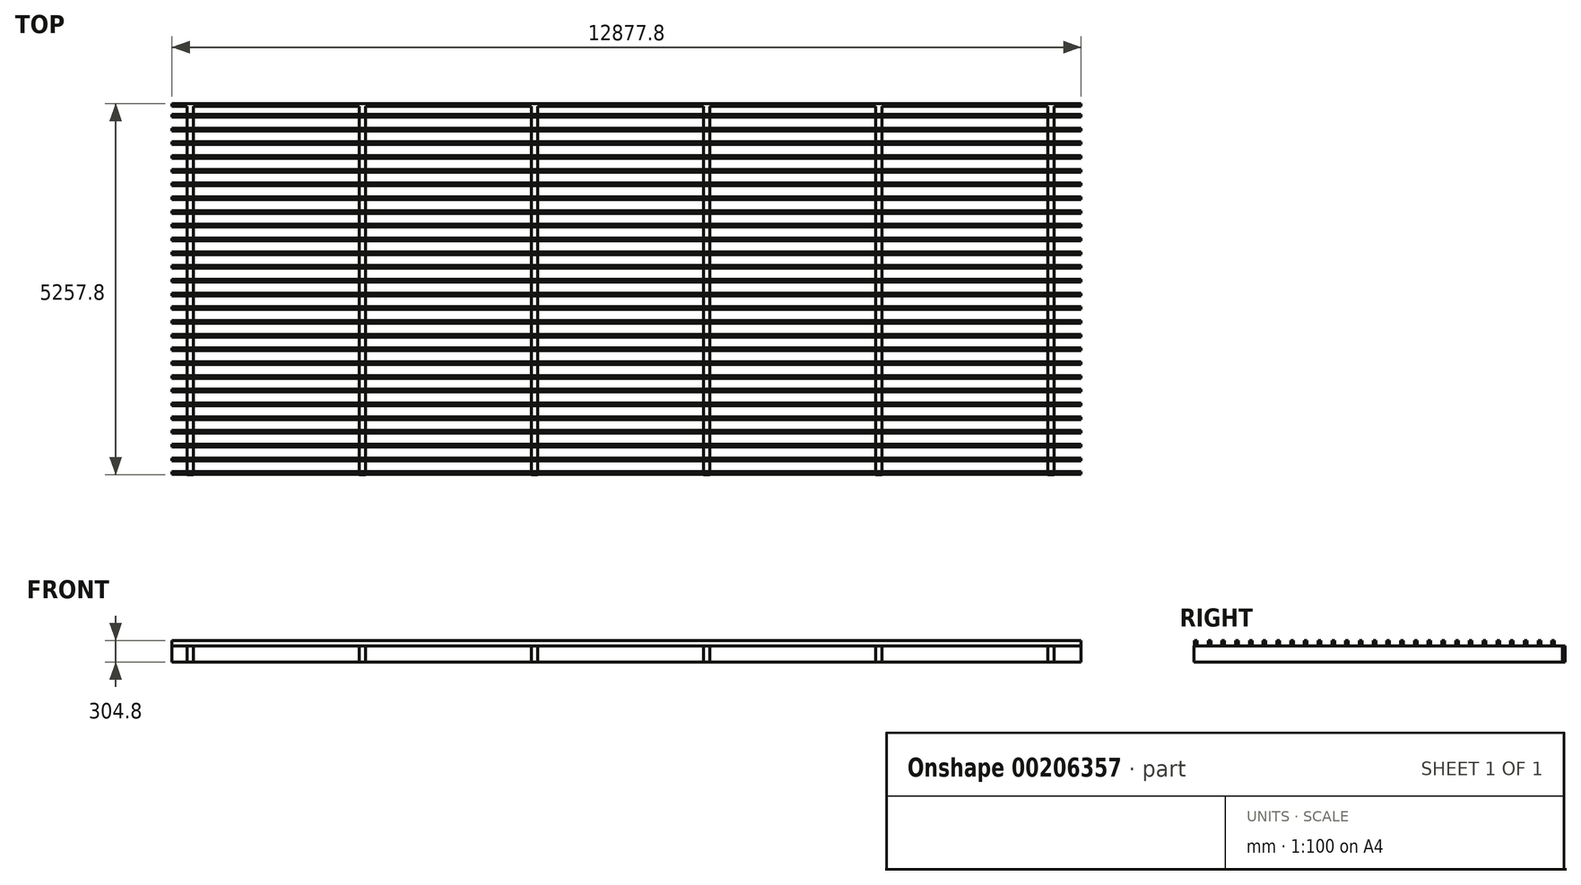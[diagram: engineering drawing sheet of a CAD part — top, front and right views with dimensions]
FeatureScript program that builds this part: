
annotation { "Feature Type Name" : "Feature", "Feature Type Description" : "" }
export const myFeature = defineFeature(function(context is Context, id is Id, definition is map)
    precondition{}
    {
        {
            var Q0;
            Q0=qCreatedBy(makeId("Front.planeOp"),FACE);
            var sketch = newSketch(context, id + "F0", { "sketchPlane" : qUnion([Q0])});
            skLineSegment(sketch, "E0.bottom", {"start": v(6438.9, -114.3) * mm, "end": v(-6438.9, -114.3) * mm});
            skLineSegment(sketch, "E0.top", {"start": v(6438.9, 114.3) * mm, "end": v(-6438.9, 114.3) * mm});
            skLineSegment(sketch, "E0.left", {"start": v(6438.9, -114.3) * mm, "end": v(6438.9, 114.3) * mm});
            skLineSegment(sketch, "E0.right", {"start": v(-6438.9, -114.3) * mm, "end": v(-6438.9, 114.3) * mm});
            skPoint(sketch, "E0.middle", {"position": v(0, 0) * mm});
            skSolve(sketch);
        }
        {
            var Q0;
            Q0 = qSketchRegion(id + "F0", true);
            extrude(context, id + "F1", {"entities" : qUnion([Q0]), "oppositeDirection" : true, "depth" : 38.1 * mm});
        }
        {
            var Q0;
            Q0=makeQuery(id+"F1.opExtrude","CAP_FACE",FACE,{"disambiguationData":[OSD([sQuery(id+"F0.wireOp",EDGE,"E0.bottom"),sQuery(id+"F0.wireOp",EDGE,"E0.top"),sQuery(id+"F0.wireOp",EDGE,"E0.left"),sQuery(id+"F0.wireOp",EDGE,"E0.right")])],"isStart":true});
            var sketch = newSketch(context, id + "F2", { "sketchPlane" : qUnion([Q0])});
            skLineSegment(sketch, "E1.bottom", {"start": v(6057.9, 114.3) * mm, "end": v(5969, 114.3) * mm});
            skLineSegment(sketch, "E1.top", {"start": v(6057.9, -114.3) * mm, "end": v(5969, -114.3) * mm});
            skLineSegment(sketch, "E1.left", {"start": v(6057.9, 114.3) * mm, "end": v(6057.9, -114.3) * mm});
            skLineSegment(sketch, "E1.right", {"start": v(5969, 114.3) * mm, "end": v(5969, -114.3) * mm});
            skLineSegment(sketch, "E2.1.0.0", {"start": v(3619.5, 114.3) * mm, "end": v(3530.6, 114.3) * mm});
            skLineSegment(sketch, "E2.1.0.1", {"start": v(3530.6, 114.3) * mm, "end": v(3530.6, -114.3) * mm});
            skLineSegment(sketch, "E2.1.0.2", {"start": v(3619.5, 114.3) * mm, "end": v(3619.5, -114.3) * mm});
            skLineSegment(sketch, "E2.1.0.3", {"start": v(3619.5, -114.3) * mm, "end": v(3530.6, -114.3) * mm});
            skLineSegment(sketch, "E2.2.0.0", {"start": v(1181.1, 114.3) * mm, "end": v(1092.2, 114.3) * mm});
            skLineSegment(sketch, "E2.2.0.1", {"start": v(1092.2, 114.3) * mm, "end": v(1092.2, -114.3) * mm});
            skLineSegment(sketch, "E2.2.0.2", {"start": v(1181.1, 114.3) * mm, "end": v(1181.1, -114.3) * mm});
            skLineSegment(sketch, "E2.2.0.3", {"start": v(1181.1, -114.3) * mm, "end": v(1092.2, -114.3) * mm});
            skLineSegment(sketch, "E2.3.0.0", {"start": v(-1257.3, 114.3) * mm, "end": v(-1346.2, 114.3) * mm});
            skLineSegment(sketch, "E2.3.0.1", {"start": v(-1346.2, 114.3) * mm, "end": v(-1346.2, -114.3) * mm});
            skLineSegment(sketch, "E2.3.0.2", {"start": v(-1257.3, 114.3) * mm, "end": v(-1257.3, -114.3) * mm});
            skLineSegment(sketch, "E2.3.0.3", {"start": v(-1257.3, -114.3) * mm, "end": v(-1346.2, -114.3) * mm});
            skLineSegment(sketch, "E2.4.0.0", {"start": v(-3695.7, 114.3) * mm, "end": v(-3784.6, 114.3) * mm});
            skLineSegment(sketch, "E2.4.0.1", {"start": v(-3784.6, 114.3) * mm, "end": v(-3784.6, -114.3) * mm});
            skLineSegment(sketch, "E2.4.0.2", {"start": v(-3695.7, 114.3) * mm, "end": v(-3695.7, -114.3) * mm});
            skLineSegment(sketch, "E2.4.0.3", {"start": v(-3695.7, -114.3) * mm, "end": v(-3784.6, -114.3) * mm});
            skLineSegment(sketch, "E2.5.0.0", {"start": v(-6134.1, 114.3) * mm, "end": v(-6223, 114.3) * mm});
            skLineSegment(sketch, "E2.5.0.1", {"start": v(-6223, 114.3) * mm, "end": v(-6223, -114.3) * mm});
            skLineSegment(sketch, "E2.5.0.2", {"start": v(-6134.1, 114.3) * mm, "end": v(-6134.1, -114.3) * mm});
            skLineSegment(sketch, "E2.5.0.3", {"start": v(-6134.1, -114.3) * mm, "end": v(-6223, -114.3) * mm});
            skLineSegment(sketch, "E2.direction1", {"start": v(5969, 114.3) * mm, "end": v(3530.6, 114.3) * mm, "construction": true});
            skSolve(sketch);
        }
        {
            var Q0;
            Q0=makeQuery(id+"F2.imprint","IMPRINT",FACE,{"disambiguationData":[TD([[makeQuery(id+"F2.imprint","IMPRINT",EDGE,{"derivedFrom":sQuery(id+"F2.wireOp",EDGE,"E2.5.0.0")}),1.0]])]});
            var Q1;
            Q1=makeQuery(id+"F2.imprint","IMPRINT",FACE,{"disambiguationData":[TD([[makeQuery(id+"F2.imprint","IMPRINT",EDGE,{"derivedFrom":sQuery(id+"F2.wireOp",EDGE,"E2.4.0.0")}),1.0]])]});
            var Q2;
            Q2=makeQuery(id+"F2.imprint","IMPRINT",FACE,{"disambiguationData":[TD([[makeQuery(id+"F2.imprint","IMPRINT",EDGE,{"derivedFrom":sQuery(id+"F2.wireOp",EDGE,"E2.3.0.0")}),1.0]])]});
            var Q3;
            Q3=makeQuery(id+"F2.imprint","IMPRINT",FACE,{"disambiguationData":[TD([[makeQuery(id+"F2.imprint","IMPRINT",EDGE,{"derivedFrom":sQuery(id+"F2.wireOp",EDGE,"E2.2.0.0")}),1.0]])]});
            var Q4;
            Q4=makeQuery(id+"F2.imprint","IMPRINT",FACE,{"disambiguationData":[TD([[makeQuery(id+"F2.imprint","IMPRINT",EDGE,{"derivedFrom":sQuery(id+"F2.wireOp",EDGE,"E2.1.0.0")}),1.0]])]});
            var Q5;
            Q5=makeQuery(id+"F2.imprint","IMPRINT",FACE,{"disambiguationData":[TD([[makeQuery(id+"F2.imprint","IMPRINT",EDGE,{"derivedFrom":sQuery(id+"F2.wireOp",EDGE,"E1.bottom")}),1.0]])]});
            extrude(context, id + "F3", {"entities" : qUnion([Q0, Q1, Q2, Q3, Q4, Q5]), "operationType" : NewBodyOperationType.ADD, "depth" : 5219.7 * mm});
        }
        {
            var Q0;
            Q0=makeQuery(id+"F1.opExtrude","SWEPT_FACE",FACE,{"disambiguationData":[OSD([sQuery(id+"F0.wireOp",EDGE,"E0.left")])]});
            var sketch = newSketch(context, id + "F4", { "sketchPlane" : qUnion([Q0])});
            skLineSegment(sketch, "E3.bottom", {"start": v(-152.4, 190.5) * mm, "end": v(-114.3, 190.5) * mm});
            skLineSegment(sketch, "E3.top", {"start": v(-152.4, 114.3) * mm, "end": v(-114.3, 114.3) * mm});
            skLineSegment(sketch, "E3.left", {"start": v(-152.4, 190.5) * mm, "end": v(-152.4, 114.3) * mm});
            skLineSegment(sketch, "E3.right", {"start": v(-114.3, 190.5) * mm, "end": v(-114.3, 114.3) * mm});
            skLineSegment(sketch, "E4.1.0.0", {"start": v(-347.14, 190.5) * mm, "end": v(-309.04, 190.5) * mm});
            skLineSegment(sketch, "E4.1.0.1", {"start": v(-347.14, 190.5) * mm, "end": v(-347.14, 114.3) * mm});
            skLineSegment(sketch, "E4.1.0.2", {"start": v(-347.14, 114.3) * mm, "end": v(-309.04, 114.3) * mm});
            skLineSegment(sketch, "E4.1.0.3", {"start": v(-309.04, 190.5) * mm, "end": v(-309.04, 114.3) * mm});
            skLineSegment(sketch, "E4.2.0.0", {"start": v(-541.88, 190.5) * mm, "end": v(-503.78, 190.5) * mm});
            skLineSegment(sketch, "E4.2.0.1", {"start": v(-541.88, 190.5) * mm, "end": v(-541.88, 114.3) * mm});
            skLineSegment(sketch, "E4.2.0.2", {"start": v(-541.88, 114.3) * mm, "end": v(-503.78, 114.3) * mm});
            skLineSegment(sketch, "E4.2.0.3", {"start": v(-503.78, 190.5) * mm, "end": v(-503.78, 114.3) * mm});
            skLineSegment(sketch, "E4.3.0.0", {"start": v(-736.63, 190.5) * mm, "end": v(-698.53, 190.5) * mm});
            skLineSegment(sketch, "E4.3.0.1", {"start": v(-736.63, 190.5) * mm, "end": v(-736.63, 114.3) * mm});
            skLineSegment(sketch, "E4.3.0.2", {"start": v(-736.63, 114.3) * mm, "end": v(-698.53, 114.3) * mm});
            skLineSegment(sketch, "E4.3.0.3", {"start": v(-698.53, 190.5) * mm, "end": v(-698.53, 114.3) * mm});
            skLineSegment(sketch, "E4.4.0.0", {"start": v(-931.37, 190.5) * mm, "end": v(-893.27, 190.5) * mm});
            skLineSegment(sketch, "E4.4.0.1", {"start": v(-931.37, 190.5) * mm, "end": v(-931.37, 114.3) * mm});
            skLineSegment(sketch, "E4.4.0.2", {"start": v(-931.37, 114.3) * mm, "end": v(-893.27, 114.3) * mm});
            skLineSegment(sketch, "E4.4.0.3", {"start": v(-893.27, 190.5) * mm, "end": v(-893.27, 114.3) * mm});
            skLineSegment(sketch, "E4.5.0.0", {"start": v(-1126.1, 190.5) * mm, "end": v(-1088, 190.5) * mm});
            skLineSegment(sketch, "E4.5.0.1", {"start": v(-1126.1, 190.5) * mm, "end": v(-1126.1, 114.3) * mm});
            skLineSegment(sketch, "E4.5.0.2", {"start": v(-1126.1, 114.3) * mm, "end": v(-1088, 114.3) * mm});
            skLineSegment(sketch, "E4.5.0.3", {"start": v(-1088, 190.5) * mm, "end": v(-1088, 114.3) * mm});
            skLineSegment(sketch, "E4.6.0.0", {"start": v(-1320.85, 190.5) * mm, "end": v(-1282.75, 190.5) * mm});
            skLineSegment(sketch, "E4.6.0.1", {"start": v(-1320.85, 190.5) * mm, "end": v(-1320.85, 114.3) * mm});
            skLineSegment(sketch, "E4.6.0.2", {"start": v(-1320.85, 114.3) * mm, "end": v(-1282.75, 114.3) * mm});
            skLineSegment(sketch, "E4.6.0.3", {"start": v(-1282.75, 190.5) * mm, "end": v(-1282.75, 114.3) * mm});
            skLineSegment(sketch, "E4.7.0.0", {"start": v(-1515.6, 190.5) * mm, "end": v(-1477.5, 190.5) * mm});
            skLineSegment(sketch, "E4.7.0.1", {"start": v(-1515.6, 190.5) * mm, "end": v(-1515.6, 114.3) * mm});
            skLineSegment(sketch, "E4.7.0.2", {"start": v(-1515.6, 114.3) * mm, "end": v(-1477.5, 114.3) * mm});
            skLineSegment(sketch, "E4.7.0.3", {"start": v(-1477.5, 190.5) * mm, "end": v(-1477.5, 114.3) * mm});
            skLineSegment(sketch, "E4.8.0.0", {"start": v(-1710.33, 190.5) * mm, "end": v(-1672.23, 190.5) * mm});
            skLineSegment(sketch, "E4.8.0.1", {"start": v(-1710.33, 190.5) * mm, "end": v(-1710.33, 114.3) * mm});
            skLineSegment(sketch, "E4.8.0.2", {"start": v(-1710.33, 114.3) * mm, "end": v(-1672.23, 114.3) * mm});
            skLineSegment(sketch, "E4.8.0.3", {"start": v(-1672.23, 190.5) * mm, "end": v(-1672.23, 114.3) * mm});
            skLineSegment(sketch, "E4.9.0.0", {"start": v(-1905.08, 190.5) * mm, "end": v(-1866.98, 190.5) * mm});
            skLineSegment(sketch, "E4.9.0.1", {"start": v(-1905.08, 190.5) * mm, "end": v(-1905.08, 114.3) * mm});
            skLineSegment(sketch, "E4.9.0.2", {"start": v(-1905.08, 114.3) * mm, "end": v(-1866.98, 114.3) * mm});
            skLineSegment(sketch, "E4.9.0.3", {"start": v(-1866.98, 190.5) * mm, "end": v(-1866.98, 114.3) * mm});
            skLineSegment(sketch, "E4.10.0.0", {"start": v(-2099.82, 190.5) * mm, "end": v(-2061.72, 190.5) * mm});
            skLineSegment(sketch, "E4.10.0.1", {"start": v(-2099.82, 190.5) * mm, "end": v(-2099.82, 114.3) * mm});
            skLineSegment(sketch, "E4.10.0.2", {"start": v(-2099.82, 114.3) * mm, "end": v(-2061.72, 114.3) * mm});
            skLineSegment(sketch, "E4.10.0.3", {"start": v(-2061.72, 190.5) * mm, "end": v(-2061.72, 114.3) * mm});
            skLineSegment(sketch, "E4.11.0.0", {"start": v(-2294.56, 190.5) * mm, "end": v(-2256.46, 190.5) * mm});
            skLineSegment(sketch, "E4.11.0.1", {"start": v(-2294.56, 190.5) * mm, "end": v(-2294.56, 114.3) * mm});
            skLineSegment(sketch, "E4.11.0.2", {"start": v(-2294.56, 114.3) * mm, "end": v(-2256.46, 114.3) * mm});
            skLineSegment(sketch, "E4.11.0.3", {"start": v(-2256.46, 190.5) * mm, "end": v(-2256.46, 114.3) * mm});
            skLineSegment(sketch, "E4.12.0.0", {"start": v(-2489.3, 190.5) * mm, "end": v(-2451.2, 190.5) * mm});
            skLineSegment(sketch, "E4.12.0.1", {"start": v(-2489.3, 190.5) * mm, "end": v(-2489.3, 114.3) * mm});
            skLineSegment(sketch, "E4.12.0.2", {"start": v(-2489.3, 114.3) * mm, "end": v(-2451.2, 114.3) * mm});
            skLineSegment(sketch, "E4.12.0.3", {"start": v(-2451.2, 190.5) * mm, "end": v(-2451.2, 114.3) * mm});
            skLineSegment(sketch, "E4.13.0.0", {"start": v(-2684.04, 190.5) * mm, "end": v(-2645.94, 190.5) * mm});
            skLineSegment(sketch, "E4.13.0.1", {"start": v(-2684.04, 190.5) * mm, "end": v(-2684.04, 114.3) * mm});
            skLineSegment(sketch, "E4.13.0.2", {"start": v(-2684.04, 114.3) * mm, "end": v(-2645.94, 114.3) * mm});
            skLineSegment(sketch, "E4.13.0.3", {"start": v(-2645.94, 190.5) * mm, "end": v(-2645.94, 114.3) * mm});
            skLineSegment(sketch, "E4.14.0.0", {"start": v(-2878.79, 190.5) * mm, "end": v(-2840.69, 190.5) * mm});
            skLineSegment(sketch, "E4.14.0.1", {"start": v(-2878.79, 190.5) * mm, "end": v(-2878.79, 114.3) * mm});
            skLineSegment(sketch, "E4.14.0.2", {"start": v(-2878.79, 114.3) * mm, "end": v(-2840.69, 114.3) * mm});
            skLineSegment(sketch, "E4.14.0.3", {"start": v(-2840.69, 190.5) * mm, "end": v(-2840.69, 114.3) * mm});
            skLineSegment(sketch, "E4.15.0.0", {"start": v(-3073.53, 190.5) * mm, "end": v(-3035.43, 190.5) * mm});
            skLineSegment(sketch, "E4.15.0.1", {"start": v(-3073.53, 190.5) * mm, "end": v(-3073.53, 114.3) * mm});
            skLineSegment(sketch, "E4.15.0.2", {"start": v(-3073.53, 114.3) * mm, "end": v(-3035.43, 114.3) * mm});
            skLineSegment(sketch, "E4.15.0.3", {"start": v(-3035.43, 190.5) * mm, "end": v(-3035.43, 114.3) * mm});
            skLineSegment(sketch, "E4.16.0.0", {"start": v(-3268.27, 190.5) * mm, "end": v(-3230.17, 190.5) * mm});
            skLineSegment(sketch, "E4.16.0.1", {"start": v(-3268.27, 190.5) * mm, "end": v(-3268.27, 114.3) * mm});
            skLineSegment(sketch, "E4.16.0.2", {"start": v(-3268.27, 114.3) * mm, "end": v(-3230.17, 114.3) * mm});
            skLineSegment(sketch, "E4.16.0.3", {"start": v(-3230.17, 190.5) * mm, "end": v(-3230.17, 114.3) * mm});
            skLineSegment(sketch, "E4.17.0.0", {"start": v(-3463.01, 190.5) * mm, "end": v(-3424.91, 190.5) * mm});
            skLineSegment(sketch, "E4.17.0.1", {"start": v(-3463.01, 190.5) * mm, "end": v(-3463.01, 114.3) * mm});
            skLineSegment(sketch, "E4.17.0.2", {"start": v(-3463.01, 114.3) * mm, "end": v(-3424.91, 114.3) * mm});
            skLineSegment(sketch, "E4.17.0.3", {"start": v(-3424.91, 190.5) * mm, "end": v(-3424.91, 114.3) * mm});
            skLineSegment(sketch, "E4.18.0.0", {"start": v(-3657.75, 190.5) * mm, "end": v(-3619.65, 190.5) * mm});
            skLineSegment(sketch, "E4.18.0.1", {"start": v(-3657.75, 190.5) * mm, "end": v(-3657.75, 114.3) * mm});
            skLineSegment(sketch, "E4.18.0.2", {"start": v(-3657.75, 114.3) * mm, "end": v(-3619.65, 114.3) * mm});
            skLineSegment(sketch, "E4.18.0.3", {"start": v(-3619.65, 190.5) * mm, "end": v(-3619.65, 114.3) * mm});
            skLineSegment(sketch, "E4.19.0.0", {"start": v(-3852.5, 190.5) * mm, "end": v(-3814.4, 190.5) * mm});
            skLineSegment(sketch, "E4.19.0.1", {"start": v(-3852.5, 190.5) * mm, "end": v(-3852.5, 114.3) * mm});
            skLineSegment(sketch, "E4.19.0.2", {"start": v(-3852.5, 114.3) * mm, "end": v(-3814.4, 114.3) * mm});
            skLineSegment(sketch, "E4.19.0.3", {"start": v(-3814.4, 190.5) * mm, "end": v(-3814.4, 114.3) * mm});
            skLineSegment(sketch, "E4.20.0.0", {"start": v(-4047.24, 190.5) * mm, "end": v(-4009.14, 190.5) * mm});
            skLineSegment(sketch, "E4.20.0.1", {"start": v(-4047.24, 190.5) * mm, "end": v(-4047.24, 114.3) * mm});
            skLineSegment(sketch, "E4.20.0.2", {"start": v(-4047.24, 114.3) * mm, "end": v(-4009.14, 114.3) * mm});
            skLineSegment(sketch, "E4.20.0.3", {"start": v(-4009.14, 190.5) * mm, "end": v(-4009.14, 114.3) * mm});
            skLineSegment(sketch, "E4.21.0.0", {"start": v(-4241.98, 190.5) * mm, "end": v(-4203.88, 190.5) * mm});
            skLineSegment(sketch, "E4.21.0.1", {"start": v(-4241.98, 190.5) * mm, "end": v(-4241.98, 114.3) * mm});
            skLineSegment(sketch, "E4.21.0.2", {"start": v(-4241.98, 114.3) * mm, "end": v(-4203.88, 114.3) * mm});
            skLineSegment(sketch, "E4.21.0.3", {"start": v(-4203.88, 190.5) * mm, "end": v(-4203.88, 114.3) * mm});
            skLineSegment(sketch, "E4.22.0.0", {"start": v(-4436.72, 190.5) * mm, "end": v(-4398.62, 190.5) * mm});
            skLineSegment(sketch, "E4.22.0.1", {"start": v(-4436.72, 190.5) * mm, "end": v(-4436.72, 114.3) * mm});
            skLineSegment(sketch, "E4.22.0.2", {"start": v(-4436.72, 114.3) * mm, "end": v(-4398.62, 114.3) * mm});
            skLineSegment(sketch, "E4.22.0.3", {"start": v(-4398.62, 190.5) * mm, "end": v(-4398.62, 114.3) * mm});
            skLineSegment(sketch, "E4.23.0.0", {"start": v(-4631.46, 190.5) * mm, "end": v(-4593.36, 190.5) * mm});
            skLineSegment(sketch, "E4.23.0.1", {"start": v(-4631.46, 190.5) * mm, "end": v(-4631.46, 114.3) * mm});
            skLineSegment(sketch, "E4.23.0.2", {"start": v(-4631.46, 114.3) * mm, "end": v(-4593.36, 114.3) * mm});
            skLineSegment(sketch, "E4.23.0.3", {"start": v(-4593.36, 190.5) * mm, "end": v(-4593.36, 114.3) * mm});
            skLineSegment(sketch, "E4.direction1", {"start": v(-152.4, 190.5) * mm, "end": v(-347.14, 190.5) * mm, "construction": true});
            skLineSegment(sketch, "E5.0.24.0", {"start": v(-4826.2, 190.5) * mm, "end": v(-4788.1, 190.5) * mm});
            skLineSegment(sketch, "E5.3.24.0", {"start": v(-4826.2, 190.5) * mm, "end": v(-4826.2, 114.3) * mm});
            skLineSegment(sketch, "E5.6.24.0", {"start": v(-4826.2, 114.3) * mm, "end": v(-4788.1, 114.3) * mm});
            skLineSegment(sketch, "E5.9.24.0", {"start": v(-4788.1, 190.5) * mm, "end": v(-4788.1, 114.3) * mm});
            skLineSegment(sketch, "E5.0.25.0", {"start": v(-5020.95, 190.5) * mm, "end": v(-4982.85, 190.5) * mm});
            skLineSegment(sketch, "E5.3.25.0", {"start": v(-5020.95, 190.5) * mm, "end": v(-5020.95, 114.3) * mm});
            skLineSegment(sketch, "E5.6.25.0", {"start": v(-5020.95, 114.3) * mm, "end": v(-4982.85, 114.3) * mm});
            skLineSegment(sketch, "E5.9.25.0", {"start": v(-4982.85, 190.5) * mm, "end": v(-4982.85, 114.3) * mm});
            skLineSegment(sketch, "E5.0.26.0", {"start": v(-5215.69, 190.5) * mm, "end": v(-5177.59, 190.5) * mm});
            skLineSegment(sketch, "E5.3.26.0", {"start": v(-5215.69, 190.5) * mm, "end": v(-5215.69, 114.3) * mm});
            skLineSegment(sketch, "E5.6.26.0", {"start": v(-5215.69, 114.3) * mm, "end": v(-5177.59, 114.3) * mm});
            skLineSegment(sketch, "E5.9.26.0", {"start": v(-5177.59, 190.5) * mm, "end": v(-5177.59, 114.3) * mm});
            skSolve(sketch);
        }
        {
            var Q0;
            Q0 = qSketchRegion(id + "F4", true);
            extrude(context, id + "F5", {"entities" : qUnion([Q0]), "operationType" : NewBodyOperationType.ADD, "oppositeDirection" : true, "depth" : 12877.8 * mm});
        }
    });
